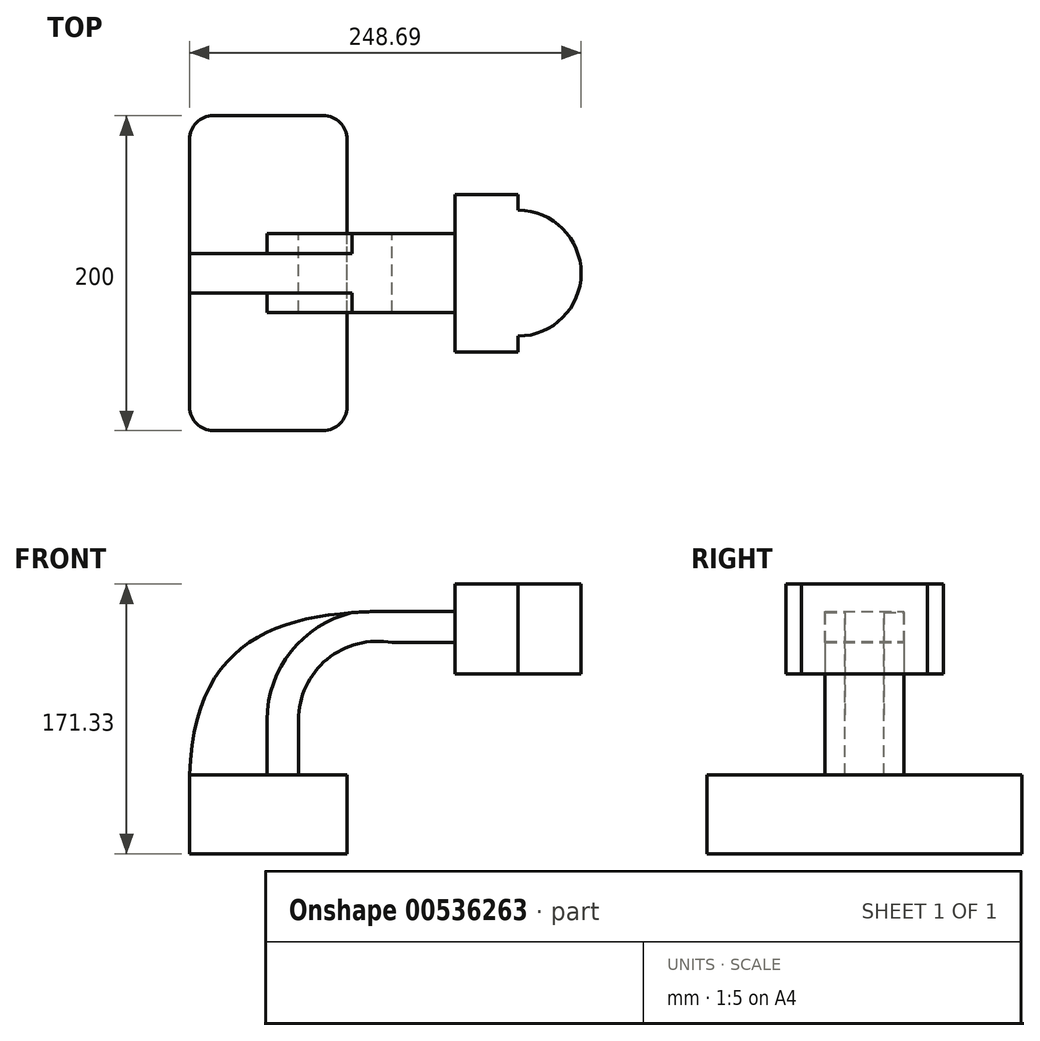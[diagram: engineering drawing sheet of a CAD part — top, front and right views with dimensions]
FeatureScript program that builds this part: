
annotation { "Feature Type Name" : "Feature", "Feature Type Description" : "" }
export const myFeature = defineFeature(function(context is Context, id is Id, definition is map)
    precondition{}
    {
        {
            var Q0;
            Q0=qCreatedBy(makeId("Front.planeOp"),FACE);
            var sketch = newSketch(context, id + "F0", { "sketchPlane" : qUnion([Q0])});
            skLineSegment(sketch, "E0.bottom", {"start": v(-50, -25) * mm, "end": v(50, -25) * mm});
            skLineSegment(sketch, "E0.top", {"start": v(-50, 25) * mm, "end": v(50, 25) * mm});
            skLineSegment(sketch, "E0.left", {"start": v(-50, -25) * mm, "end": v(-50, 25) * mm});
            skLineSegment(sketch, "E0.right", {"start": v(50, -25) * mm, "end": v(50, 25) * mm});
            skPoint(sketch, "E0.middle", {"position": v(0, 0) * mm});
            skLineSegment(sketch, "E1.bottom", {"start": v(118.7, 89.1) * mm, "end": v(158.7, 89.1) * mm});
            skLineSegment(sketch, "E1.top", {"start": v(118.7, 146.33) * mm, "end": v(158.7, 146.33) * mm});
            skLineSegment(sketch, "E1.left", {"start": v(118.7, 89.1) * mm, "end": v(118.7, 146.33) * mm});
            skLineSegment(sketch, "E1.right", {"start": v(158.7, 89.1) * mm, "end": v(158.7, 146.33) * mm});
            skPoint(sketch, "E1.middle", {"position": v(138.7, 117.71) * mm});
            skLineSegment(sketch, "E2", {"start": v(19.23, 25) * mm, "end": v(19.23, 60) * mm});
            skArc(sketch, "E3", {"start": v(19.23, 60) * mm, "mid": v(37.4, 98.55) * mm, "end": v(78.7, 109.1) * mm});
            skPoint(sketch, "E4.endSnap0", {"position": v(138.7, 89.1) * mm});
            skLineSegment(sketch, "E5", {"start": v(78.7, 109.1) * mm, "end": v(118.7, 109.1) * mm});
            skLineSegment(sketch, "E6.0", {"start": v(80.44, 129.1) * mm, "end": v(119.59, 129.1) * mm});
            skArc(sketch, "E6.1", {"start": v(-0.77, 60) * mm, "mid": v(23.87, 113.31) * mm, "end": v(80.44, 129.1) * mm});
            skLineSegment(sketch, "E6.2", {"start": v(-0.77, 25) * mm, "end": v(-0.77, 60) * mm});
            skFitSpline(sketch, "E7", {"points": [v(-50, 25) * mm, v(80.44, 129.1) * mm], "startDerivative": vector(9.68, 262.4) * mm, "endDerivative": vector(220.78, 0) * mm});
            skSolve(sketch);
        }
        {
            var Q0;
            Q0=makeQuery(id+"F0.imprint","IMPRINT",FACE,{"disambiguationData":[TD([[makeQuery(id+"F0.imprint","IMPRINT",EDGE,{"derivedFrom":sQuery(id+"F0.wireOp",EDGE,"E0.bottom")}),1.0]])]});
            extrude(context, id + "F1", {"entities" : qUnion([Q0]), "endBound" : BoundingType.SYMMETRIC, "depth" : 200 * mm, "offsetDistance" : 25 * mm});
        }
        {
            var Q0;
            {var subQ0=sQuery(id+"F0.wireOp",EDGE,"E2");Q0=makeQuery(id+"F0.imprint","IMPRINT",FACE,{"disambiguationData":[TD([[makeQuery(id+"F0.imprint","IMPRINT",EDGE,{"derivedFrom":subQ0}),1.0]])]});}
            extrude(context, id + "F2", {"entities" : qUnion([Q0]), "operationType" : NewBodyOperationType.ADD, "endBound" : BoundingType.SYMMETRIC, "depth" : 50 * mm, "offsetDistance" : 25 * mm});
        }
        {
            var Q0;
            {var subQ3=sQuery(id+"F0.wireOp",EDGE,"E1.bottom");Q0=makeQuery(id+"F0.imprint","IMPRINT",FACE,{"disambiguationData":[TD([[makeQuery(id+"F0.imprint","IMPRINT",EDGE,{"derivedFrom":subQ3}),1.0]])]});}
            extrude(context, id + "F3", {"entities" : qUnion([Q0]), "operationType" : NewBodyOperationType.ADD, "endBound" : BoundingType.SYMMETRIC, "depth" : 100 * mm, "offsetDistance" : 25 * mm});
        }
        {
            var Q0;
            {var subQ3=sQuery(id+"F0.wireOp",EDGE,"E1.bottom");Q0=makeQuery(id+"F0.imprint","IMPRINT",FACE,{"disambiguationData":[TD([[makeQuery(id+"F0.imprint","IMPRINT",EDGE,{"derivedFrom":subQ3}),1.0]])]});}
            var Q1;
            Q1=makeQuery(id+"F3.opExtrude","CAP_EDGE",EDGE,{"disambiguationData":[OSD([sQuery(id+"F0.wireOp",EDGE,"E1.right")])],"isStart":false});
            var Q2;
            Q2=sQuery(id+"F0.wireOp",EDGE,"E1.right");
            revolve(context, id + "F4", {"operationType" : NewBodyOperationType.ADD, "entities" : qUnion([Q0]), "surfaceEntities" : qUnion([Q1]), "axis" : qUnion([Q2]), "revolveType" : RevolveType.FULL, "oppositeDirection" : true});
        }
        {
            var Q0;
            {var subQ3=sQuery(id+"F0.wireOp",EDGE,"E6.2");Q0=makeQuery(id+"F0.imprint","IMPRINT",FACE,{"disambiguationData":[TD([[makeQuery(id+"F0.imprint","IMPRINT",EDGE,{"derivedFrom":subQ3}),1.0]])]});}
            extrude(context, id + "F5", {"entities" : qUnion([Q0]), "operationType" : NewBodyOperationType.ADD, "endBound" : BoundingType.SYMMETRIC, "depth" : 25 * mm, "offsetDistance" : 25 * mm});
        }
        {
            var Q0;
            Q0=makeQuery(id+"F1.opExtrude","CAP_EDGE",EDGE,{"disambiguationData":[OSD([sQuery(id+"F0.wireOp",EDGE,"E0.left")])],"isStart":false});
            var Q1;
            Q1=makeQuery(id+"F1.opExtrude","CAP_EDGE",EDGE,{"disambiguationData":[OSD([sQuery(id+"F0.wireOp",EDGE,"E0.right")])],"isStart":false});
            var Q2;
            Q2=makeQuery(id+"F1.opExtrude","CAP_EDGE",EDGE,{"disambiguationData":[OSD([sQuery(id+"F0.wireOp",EDGE,"E0.right")])],"isStart":true});
            var Q3;
            Q3=makeQuery(id+"F1.opExtrude","CAP_EDGE",EDGE,{"disambiguationData":[OSD([sQuery(id+"F0.wireOp",EDGE,"E0.left")])],"isStart":true});
            fillet(context, id + "F6", {"entities" : qUnion([Q0, Q1, Q2, Q3]), "radius" : 15 * mm, "tangentPropagation" : true, "allowEdgeOverflow" : false});
        }
    });
